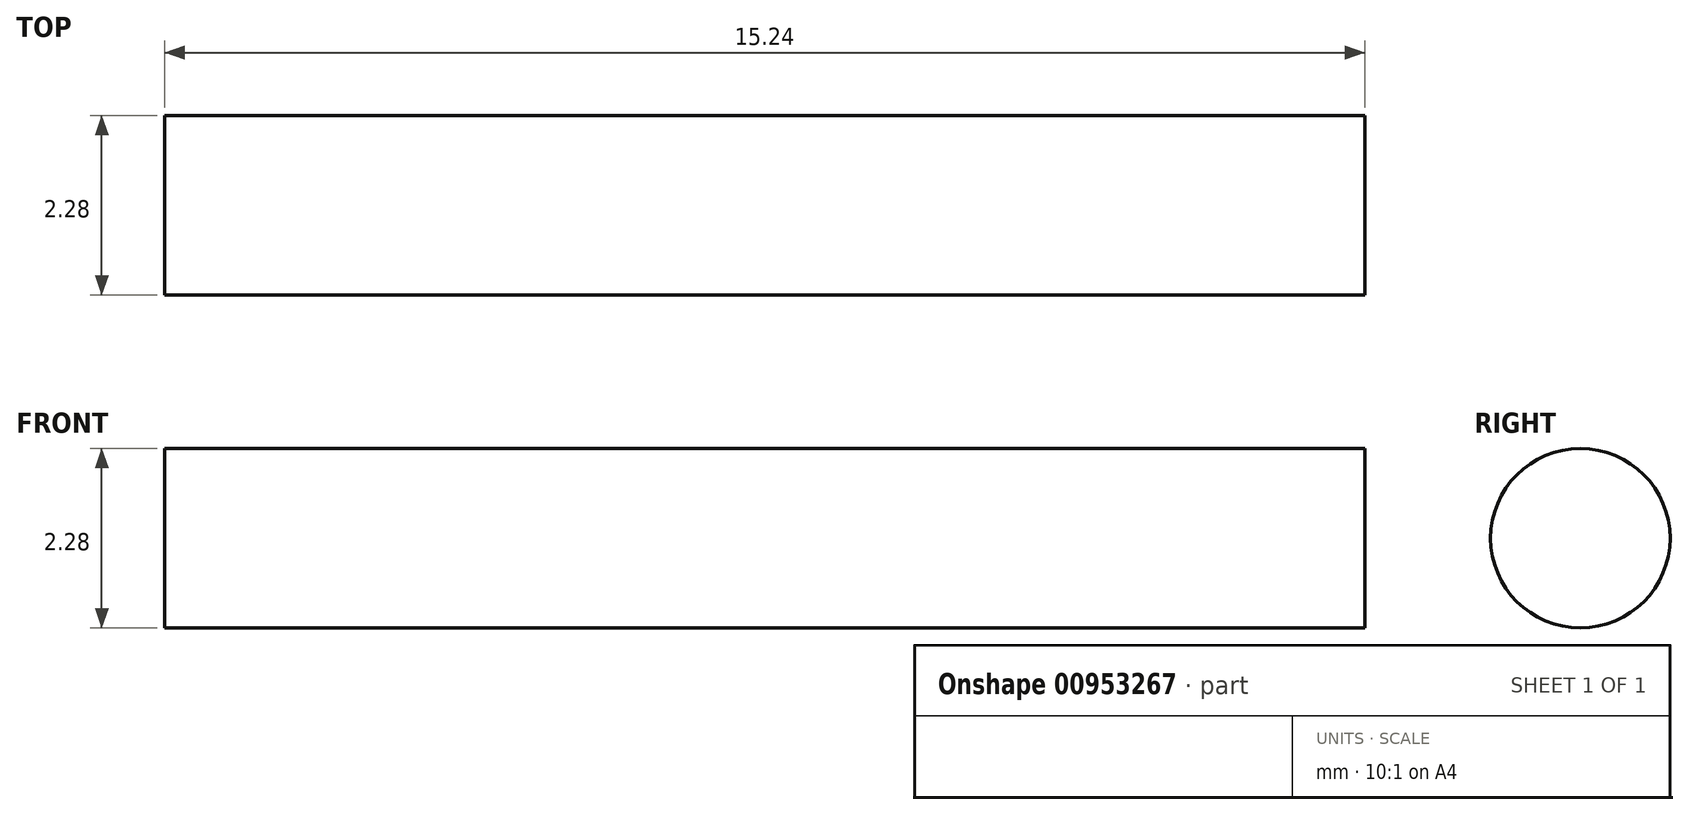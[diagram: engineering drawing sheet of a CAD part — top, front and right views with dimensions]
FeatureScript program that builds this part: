
annotation { "Feature Type Name" : "Feature", "Feature Type Description" : "" }
export const myFeature = defineFeature(function(context is Context, id is Id, definition is map)
    precondition{}
    {
        {
            var Q0;
            Q0=qCreatedBy(makeId("Right.planeOp"),FACE);
            var sketch = newSketch(context, id + "F0", { "sketchPlane" : qUnion([Q0])});
            skCircle(sketch, "E0", {"center": v(0, 0) * mm, "radius": 1.14 * mm});
            skSolve(sketch);
        }
        {
            var Q0;
            Q0 = qSketchRegion(id + "F0", true);
            extrude(context, id + "F1", {"entities" : qUnion([Q0]), "endBound" : BoundingType.SYMMETRIC, "depth" : 15.24 * mm, "offsetDistance" : 25 * mm});
        }
        {
            var Q0;
            Q0=qCreatedBy(makeId("Right.planeOp"),FACE);
            var sketch = newSketch(context, id + "F2", { "sketchPlane" : qUnion([Q0])});
            skCircle(sketch, "E1", {"center": v(0, 0) * mm, "radius": 0.38 * mm});
            skSolve(sketch);
        }
        {
            var Q0;
            Q0=sQuery(id+"F2.wireOp",EDGE,"E1");
            extrude(context, id + "F3", {"bodyType" : ToolBodyType.SURFACE, "surfaceEntities" : qUnion([Q0]), "endBound" : BoundingType.SYMMETRIC, "depth" : 17.52 * mm, "offsetDistance" : 25 * mm});
        }
    });
